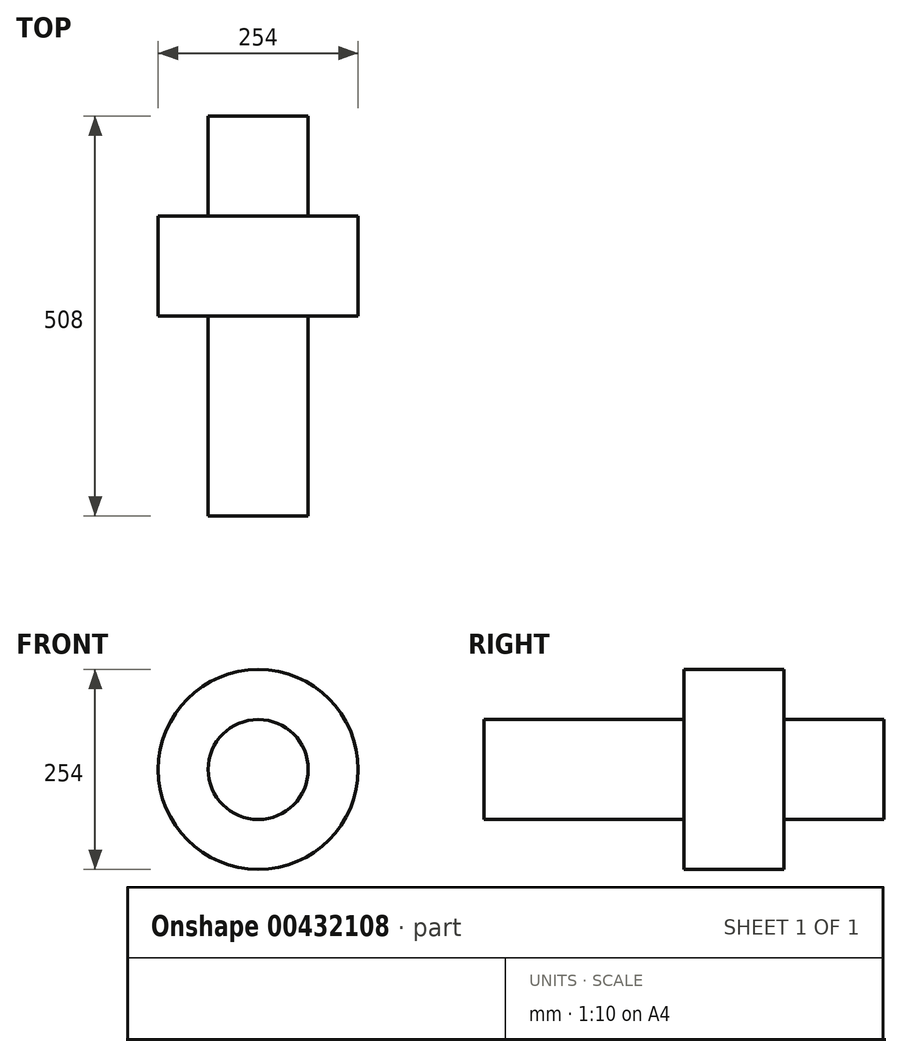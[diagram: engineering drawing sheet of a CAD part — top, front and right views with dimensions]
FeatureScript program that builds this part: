
annotation { "Feature Type Name" : "Feature", "Feature Type Description" : "" }
export const myFeature = defineFeature(function(context is Context, id is Id, definition is map)
    precondition{}
    {
        {
            var Q0;
            Q0=qCreatedBy(makeId("Front.planeOp"),FACE);
            var sketch = newSketch(context, id + "F0", { "sketchPlane" : qUnion([Q0])});
            skCircle(sketch, "E0", {"center": v(0, 0) * mm, "radius": 63.5 * mm});
            skSolve(sketch);
        }
        {
            var Q0;
            Q0 = qSketchRegion(id + "F0", true);
            extrude(context, id + "F1", {"entities" : qUnion([Q0]), "depth" : 508 * mm});
        }
        {
            var Q0;
            Q0=qCreatedBy(makeId("Front.planeOp"),FACE);
            cPlane(context, id + "F2", {"entities" : qUnion([Q0]), "cplaneType" : CPlaneType.OFFSET, "offset" : 127 * mm, "width" : 152.4 * mm, "height" : 152.4 * mm});
        }
        {
            var Q0;
            Q0=qCreatedBy(id+"F2.planeOp",FACE);
            var sketch = newSketch(context, id + "F3", { "sketchPlane" : qUnion([Q0])});
            skCircle(sketch, "E1", {"center": v(0, 0) * mm, "radius": 127 * mm});
            skSolve(sketch);
        }
        {
            var Q0;
            Q0 = qSketchRegion(id + "F3", true);
            extrude(context, id + "F4", {"entities" : qUnion([Q0]), "operationType" : NewBodyOperationType.ADD, "depth" : 127 * mm});
        }
    });
